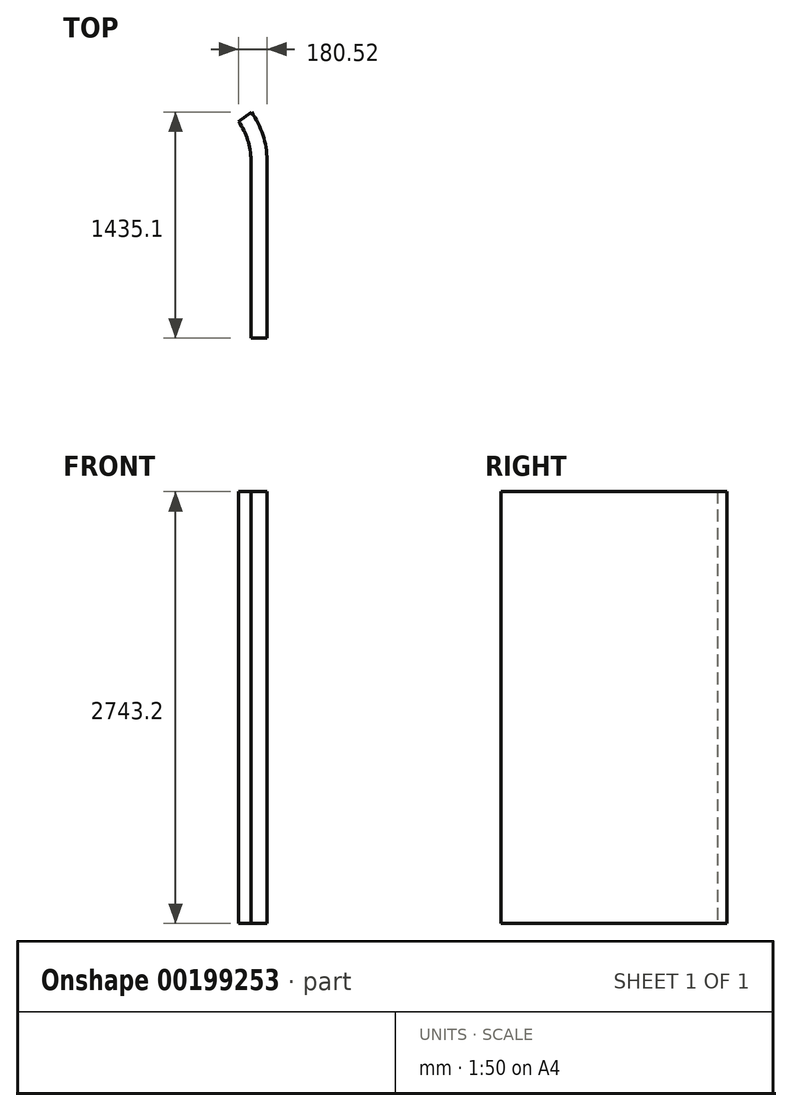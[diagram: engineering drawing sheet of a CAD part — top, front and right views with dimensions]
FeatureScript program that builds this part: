
annotation { "Feature Type Name" : "Feature", "Feature Type Description" : "" }
export const myFeature = defineFeature(function(context is Context, id is Id, definition is map)
    precondition{}
    {
        {
            var Q0;
            Q0=qCreatedBy(makeId("Top.planeOp"),FACE);
            var sketch = newSketch(context, id + "F0", { "sketchPlane" : qUnion([Q0])});
            skLineSegment(sketch, "E0", {"start": v(-2316.67, 229.42) * mm, "end": v(349.93, 229.42) * mm});
            skLineSegment(sketch, "E1", {"start": v(2064.43, -1485.08) * mm, "end": v(2064.43, -2094.68) * mm});
            skArc(sketch, "E2", {"start": v(2064.43, -1485.08) * mm, "mid": v(852.1, -982.92) * mm, "end": v(349.93, 229.42) * mm});
            skArc(sketch, "E3.0", {"start": v(2064.43, -1789.88) * mm, "mid": v(1189.8, -1590.64) * mm, "end": v(487.77, -1032.22) * mm});
            skArc(sketch, "E4.0", {"start": v(2064.43, -2094.68) * mm, "mid": v(1057.78, -1865.36) * mm, "end": v(249.79, -1222.65) * mm});
            skLineSegment(sketch, "E5", {"start": v(-2316.67, 229.42) * mm, "end": v(-2345.78, -77.56) * mm});
            skPoint(sketch, "E6", {"position": v(-2316.67, 229.42) * mm});
            skArc(sketch, "E7", {"start": v(487.77, -1032.22) * mm, "mid": v(-608.98, -137.02) * mm, "end": v(-1976.45, 229.42) * mm});
            skArc(sketch, "E8.0", {"start": v(249.79, -1222.65) * mm, "mid": v(-907.75, -332.21) * mm, "end": v(-2345.78, -77.56) * mm});
            skPoint(sketch, "E9.orphan", {"position": v(-2436.3, -1032.22) * mm});
            skLineSegment(sketch, "E10", {"start": v(-2343.36, -51.95) * mm, "end": v(-2316.67, 229.42) * mm});
            skLineSegment(sketch, "E11", {"start": v(-2291.3, 227.87) * mm, "end": v(-2316.67, 229.42) * mm});
            skLineSegment(sketch, "E12.bottom", {"start": v(2039.03, -1484.9) * mm, "end": v(2064.43, -1484.9) * mm});
            skLineSegment(sketch, "E12.top", {"start": v(2039.03, -1485.08) * mm, "end": v(2064.43, -1485.08) * mm});
            skLineSegment(sketch, "E12.left", {"start": v(2039.03, -1484.9) * mm, "end": v(2039.03, -1485.08) * mm});
            skLineSegment(sketch, "E12.right", {"start": v(2064.43, -1484.9) * mm, "end": v(2064.43, -1485.08) * mm});
            skLineSegment(sketch, "E13.0", {"start": v(2166.03, -1485.08) * mm, "end": v(2166.03, -2094.68) * mm});
            skLineSegment(sketch, "E14", {"start": v(2064.43, -2094.68) * mm, "end": v(2166.03, -2094.68) * mm});
            skLineSegment(sketch, "E15", {"start": v(2166.03, -1485.08) * mm, "end": v(2166.03, -1231.08) * mm});
            skLineSegment(sketch, "E16", {"start": v(2166.03, -2094.68) * mm, "end": v(2166.03, -2361.38) * mm});
            skLineSegment(sketch, "E17", {"start": v(2064.43, -2094.68) * mm, "end": v(2064.43, -2361.38) * mm});
            skLineSegment(sketch, "E18", {"start": v(2166.03, -2361.38) * mm, "end": v(2064.43, -2361.38) * mm});
            skPoint(sketch, "E19.orphan", {"position": v(2064.43, -468.9) * mm});
            skPoint(sketch, "E20", {"position": v(2166.03, -1231.08) * mm});
            skLineSegment(sketch, "E21", {"start": v(2166.03, -1231.08) * mm, "end": v(2166.03, -926.28) * mm});
            skLineSegment(sketch, "E22", {"start": v(2067.25, -926.28) * mm, "end": v(2166.03, -926.28) * mm});
            skPoint(sketch, "E23", {"position": v(2166.03, -1485.08) * mm});
            skPoint(sketch, "E24", {"position": v(2166.03, -2094.68) * mm});
            skArc(sketch, "E25", {"start": v(2166.03, -1231.08) * mm, "mid": v(2140.72, -1070.88) * mm, "end": v(2067.25, -926.28) * mm});
            skArc(sketch, "E26.0", {"start": v(2064.43, -1231.08) * mm, "mid": v(2044.2, -1102.64) * mm, "end": v(1985.51, -986.63) * mm});
            skLineSegment(sketch, "E27", {"start": v(2064.43, -1484.9) * mm, "end": v(2064.43, -1231.08) * mm});
            skLineSegment(sketch, "E28", {"start": v(2067.25, -926.28) * mm, "end": v(1985.51, -986.63) * mm});
            skSolve(sketch);
        }
        {
            var Q0;
            Q0=makeQuery(id+"F0.imprint","IMPRINT",FACE,{"disambiguationData":[TD([[makeQuery(id+"F0.imprint","IMPRINT",EDGE,{"derivedFrom":sQuery(id+"F0.wireOp",EDGE,"E14")}),-1.0]])]});
            var Q1;
            {var subQ3=sQuery(id+"F0.wireOp",EDGE,"E12.right");Q1=makeQuery(id+"F0.imprint","IMPRINT",FACE,{"disambiguationData":[TD([[makeQuery(id+"F0.imprint","IMPRINT",EDGE,{"derivedFrom":subQ3}),1.0]])]});}
            extrude(context, id + "F1", {"entities" : qUnion([Q0, Q1]), "depth" : 2743.2 * mm});
        }
    });
